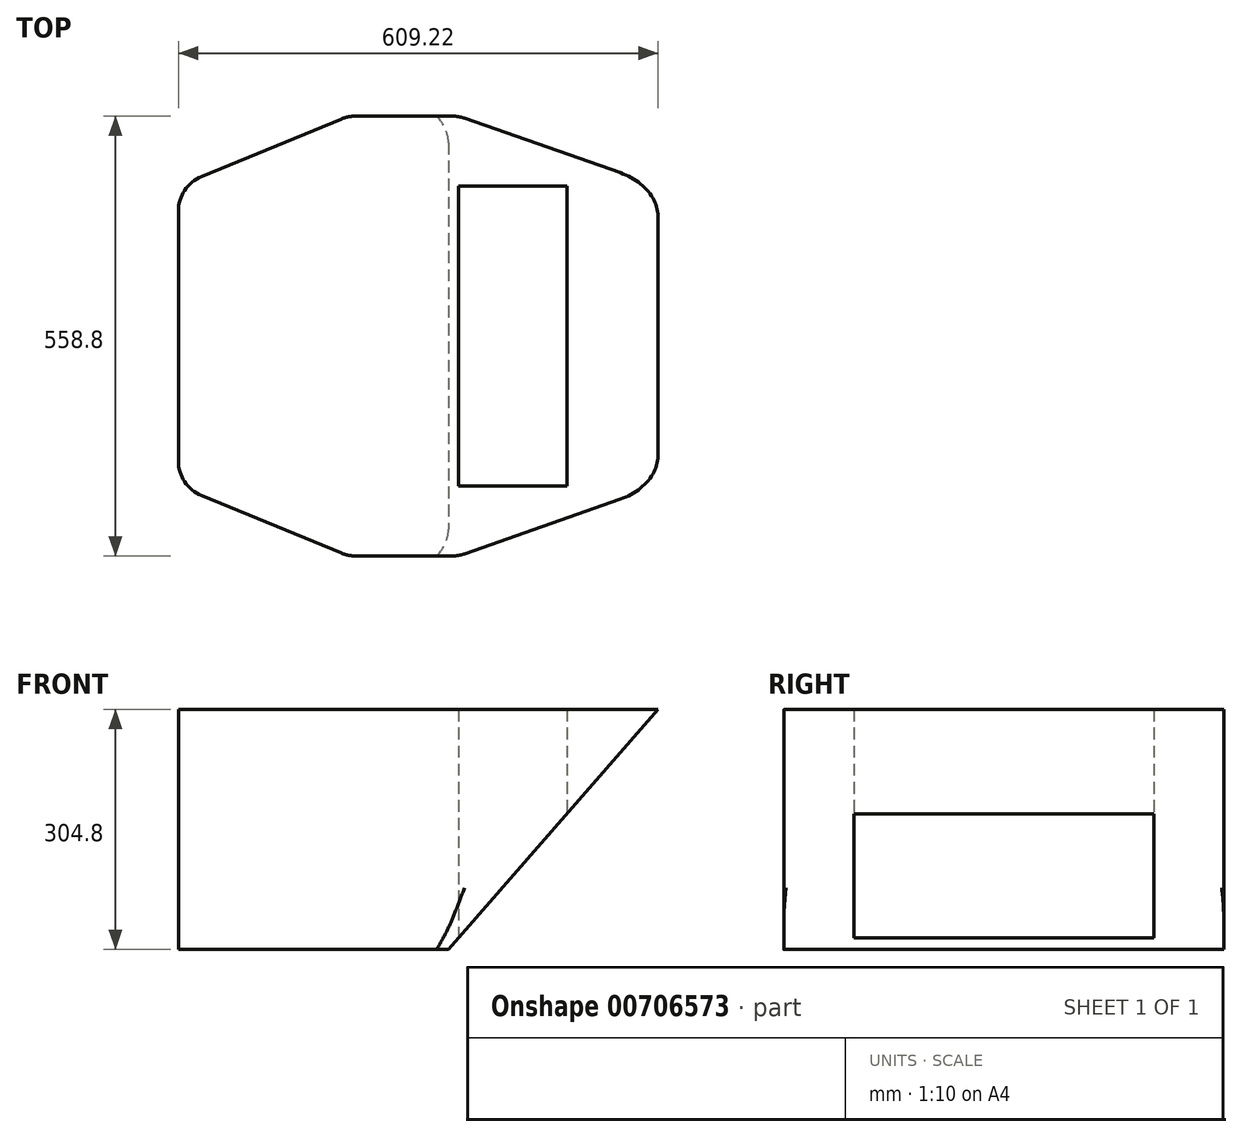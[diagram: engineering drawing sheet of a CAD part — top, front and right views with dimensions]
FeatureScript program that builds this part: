
annotation { "Feature Type Name" : "Feature", "Feature Type Description" : "" }
export const myFeature = defineFeature(function(context is Context, id is Id, definition is map)
    precondition{}
    {
        {
            var Q0;
            Q0=qCreatedBy(makeId("Top.planeOp"),FACE);
            var sketch = newSketch(context, id + "F0", { "sketchPlane" : qUnion([Q0])});
            skLineSegment(sketch, "E0.bottom", {"start": v(50.8, 279.4) * mm, "end": v(-88.9, 279.4) * mm});
            skLineSegment(sketch, "E0.top", {"start": v(50.8, -279.4) * mm, "end": v(-88.9, -279.4) * mm});
            skLineSegment(sketch, "E0.left", {"start": v(188.62, 231.16) * mm, "end": v(188.62, -231.16) * mm});
            skPoint(sketch, "E0.middle", {"position": v(0, 0) * mm});
            skLineSegment(sketch, "E1.left", {"start": v(304.8, 190.5) * mm, "end": v(304.8, -190.5) * mm});
            skLineSegment(sketch, "E1.right", {"start": v(-304.8, 190.5) * mm, "end": v(-304.8, -190.5) * mm});
            skLineSegment(sketch, "E2", {"start": v(0, 0) * mm, "end": v(-304.8, 0) * mm});
            skLineSegment(sketch, "E3.bottom", {"start": v(-188.62, 0) * mm, "end": v(-88.9, 0) * mm});
            skLineSegment(sketch, "E3.left", {"start": v(-304.8, 0) * mm, "end": v(-304.8, 190.5) * mm});
            skLineSegment(sketch, "E3.right", {"start": v(-88.9, 0) * mm, "end": v(-88.9, 190.5) * mm});
            skLineSegment(sketch, "E4.bottom", {"start": v(-304.8, 0) * mm, "end": v(-88.9, 0) * mm});
            skLineSegment(sketch, "E4.left", {"start": v(-304.8, 0) * mm, "end": v(-304.8, -190.5) * mm});
            skLineSegment(sketch, "E4.right", {"start": v(-88.9, 0) * mm, "end": v(-88.9, -190.5) * mm});
            skLineSegment(sketch, "E5", {"start": v(-88.9, 190.5) * mm, "end": v(-88.9, 279.4) * mm});
            skLineSegment(sketch, "E6", {"start": v(-88.9, -190.5) * mm, "end": v(-88.9, -279.4) * mm});
            skLineSegment(sketch, "E7", {"start": v(-88.9, -279.4) * mm, "end": v(-304.8, -190.5) * mm});
            skLineSegment(sketch, "E8", {"start": v(-304.8, 190.5) * mm, "end": v(-88.9, 279.4) * mm});
            skLineSegment(sketch, "E9.trimOffspring", {"start": v(-88.9, 0) * mm, "end": v(304.8, 0) * mm});
            skPoint(sketch, "E10.orphan", {"position": v(-304.8, -279.4) * mm});
            skPoint(sketch, "E11.orphan", {"position": v(-188.62, -279.4) * mm});
            skPoint(sketch, "E12.trimOffspring.start.orphan", {"position": v(-188.62, 279.4) * mm});
            skPoint(sketch, "E13.orphan", {"position": v(-304.8, 279.4) * mm});
            skLineSegment(sketch, "E14.bottom", {"start": v(304.8, 0) * mm, "end": v(50.8, 0) * mm});
            skLineSegment(sketch, "E14.top", {"start": v(304.8, 190.5) * mm, "end": v(50.8, 190.5) * mm});
            skLineSegment(sketch, "E14.left", {"start": v(304.8, 0) * mm, "end": v(304.8, 190.5) * mm});
            skLineSegment(sketch, "E14.right", {"start": v(50.8, 0) * mm, "end": v(50.8, 190.5) * mm});
            skLineSegment(sketch, "E15", {"start": v(50.8, -190.5) * mm, "end": v(304.8, -190.5) * mm});
            skLineSegment(sketch, "E16", {"start": v(50.8, 0) * mm, "end": v(50.8, -190.5) * mm});
            skLineSegment(sketch, "E17", {"start": v(50.8, 190.5) * mm, "end": v(50.8, 279.4) * mm});
            skLineSegment(sketch, "E18", {"start": v(50.8, 279.4) * mm, "end": v(304.8, 190.5) * mm});
            skPoint(sketch, "E19.orphan", {"position": v(188.62, 279.4) * mm});
            skPoint(sketch, "E20.orphan", {"position": v(304.8, 279.4) * mm});
            skLineSegment(sketch, "E21", {"start": v(50.8, -190.5) * mm, "end": v(50.8, -279.4) * mm});
            skLineSegment(sketch, "E22", {"start": v(50.8, -279.4) * mm, "end": v(304.8, -190.5) * mm});
            skPoint(sketch, "E23.orphan", {"position": v(304.8, -279.4) * mm});
            skPoint(sketch, "E24.orphan", {"position": v(188.62, -279.4) * mm});
            skSolve(sketch);
        }
        {
            var Q0;
            Q0 = qSketchRegion(id + "F0", true);
            extrude(context, id + "F1", {"entities" : qUnion([Q0]), "depth" : 304.8 * mm, "offsetDistance" : 25.4 * mm});
        }
        {
            var Q0;
            Q0=qCreatedBy(makeId("Front.planeOp"),FACE);
            var sketch = newSketch(context, id + "F2", { "sketchPlane" : qUnion([Q0])});
            skLineSegment(sketch, "E25", {"start": v(38.2, 0) * mm, "end": v(306.47, 307.14) * mm});
            skLineSegment(sketch, "E26", {"start": v(306.47, 307.14) * mm, "end": v(306.47, -19.84) * mm});
            skLineSegment(sketch, "E27", {"start": v(306.47, -19.84) * mm, "end": v(6, -19.84) * mm});
            skLineSegment(sketch, "E28", {"start": v(6, -19.84) * mm, "end": v(42.6, 0) * mm});
            skLineSegment(sketch, "E29", {"start": v(42.6, 0) * mm, "end": v(-147.4, -79.8) * mm});
            skLineSegment(sketch, "E30", {"start": v(-147.4, -79.8) * mm, "end": v(38.2, 0) * mm});
            skSolve(sketch);
        }
        {
            var Q0;
            Q0 = qSketchRegion(id + "F2", true);
            extrude(context, id + "F3", {"entities" : qUnion([Q0]), "operationType" : NewBodyOperationType.REMOVE, "oppositeDirection" : true, "depth" : 401.32 * mm, "offsetDistance" : 25.4 * mm});
        }
        {
            var Q0;
            Q0 = qSketchRegion(id + "F2", true);
            extrude(context, id + "F4", {"entities" : qUnion([Q0]), "operationType" : NewBodyOperationType.REMOVE, "depth" : 942.34 * mm, "offsetDistance" : 25.4 * mm});
        }
        {
            var Q0;
            Q0=makeQuery(id+"F1.opExtrude","SWEPT_EDGE",EDGE,{"disambiguationData":[OSD([sQuery(id+"F0.wireOp",EDGE,"E0.bottom"),sQuery(id+"F0.wireOp",EDGE,"E17"),sQuery(id+"F0.wireOp",EDGE,"E18")])]});
            var Q1;
            Q1=makeQuery(id+"F1.opExtrude","SWEPT_EDGE",EDGE,{"disambiguationData":[OSD([sQuery(id+"F0.wireOp",EDGE,"E0.bottom"),sQuery(id+"F0.wireOp",EDGE,"E5"),sQuery(id+"F0.wireOp",EDGE,"E8")])]});
            var Q2;
            Q2=makeQuery(id+"F1.opExtrude","SWEPT_EDGE",EDGE,{"disambiguationData":[OSD([sQuery(id+"F0.wireOp",EDGE,"E3.left"),sQuery(id+"F0.wireOp",EDGE,"E8")])]});
            var Q3;
            Q3=makeQuery(id+"F1.opExtrude","SWEPT_EDGE",EDGE,{"disambiguationData":[OSD([sQuery(id+"F0.wireOp",EDGE,"E6"),sQuery(id+"F0.wireOp",EDGE,"E7"),sQuery(id+"F0.wireOp",EDGE,"E0.top")])]});
            var Q4;
            Q4=makeQuery(id+"F1.opExtrude","SWEPT_EDGE",EDGE,{"disambiguationData":[OSD([sQuery(id+"F0.wireOp",EDGE,"E21"),sQuery(id+"F0.wireOp",EDGE,"E22"),sQuery(id+"F0.wireOp",EDGE,"E0.top")])]});
            var Q5;
            Q5=makeQuery(id+"F1.opExtrude","SWEPT_EDGE",EDGE,{"disambiguationData":[OSD([sQuery(id+"F0.wireOp",EDGE,"E4.left"),sQuery(id+"F0.wireOp",EDGE,"E7")])]});
            var Q6;
            Q6=makeQuery(id+"F3.boolean.opBoolean","INTERSECT",EDGE,{"derivedFrom":[makeQuery(id+"F1.opExtrude","SWEPT_FACE",FACE,{"disambiguationData":[OSD([sQuery(id+"F0.wireOp",EDGE,"E18")])]}),makeQuery(id+"F3.opExtrude","SWEPT_FACE",FACE,{"disambiguationData":[OSD([sQuery(id+"F2.wireOp",EDGE,"E25")])]})]});
            var Q7;
            Q7=makeQuery(id+"F4.boolean.opBoolean","INTERSECT",EDGE,{"derivedFrom":[makeQuery(id+"F1.opExtrude","SWEPT_FACE",FACE,{"disambiguationData":[OSD([sQuery(id+"F0.wireOp",EDGE,"E22")])]}),makeQuery(id+"F4.opExtrude","SWEPT_FACE",FACE,{"disambiguationData":[OSD([sQuery(id+"F2.wireOp",EDGE,"E25")])]})]});
            fillet(context, id + "F5", {"entities" : qUnion([Q0, Q1, Q2, Q3, Q4, Q5, Q6, Q7]), "radius" : 47.83 * mm, "tangentPropagation" : true, "allowEdgeOverflow" : false});
        }
    });
